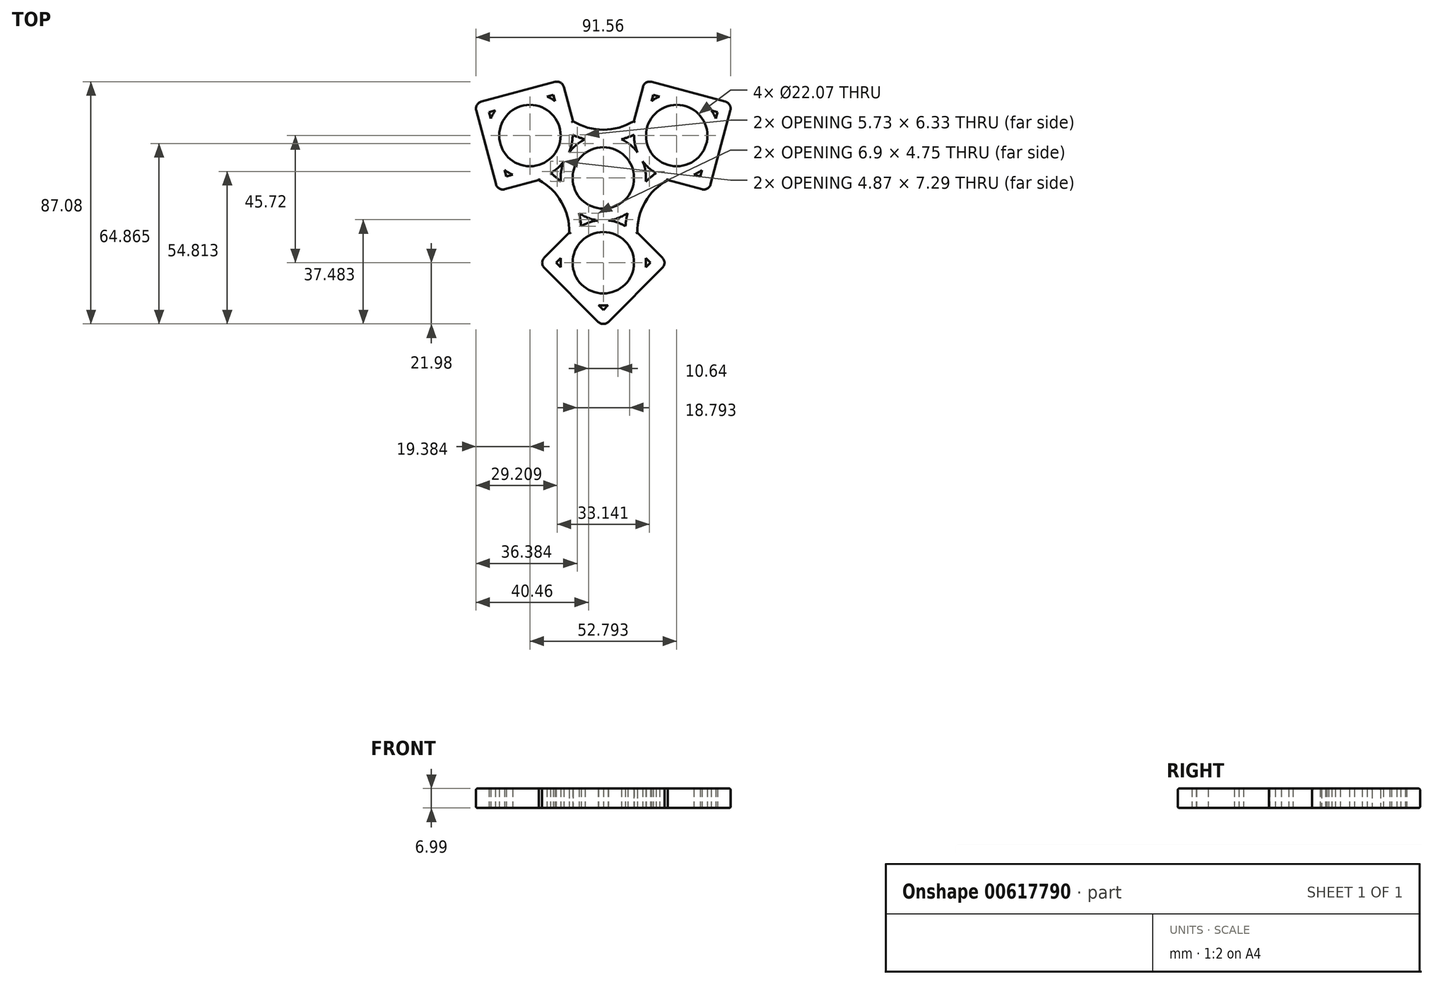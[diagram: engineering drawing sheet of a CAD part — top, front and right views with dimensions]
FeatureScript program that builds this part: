
annotation { "Feature Type Name" : "Feature", "Feature Type Description" : "" }
export const myFeature = defineFeature(function(context is Context, id is Id, definition is map)
    precondition{}
    {
        {
            var Q0;
            Q0=qCreatedBy(makeId("Top.planeOp"),FACE);
            var sketch = newSketch(context, id + "F0", { "sketchPlane" : qUnion([Q0])});
            skCircle(sketch, "E0", {"center": v(0, 0) * mm, "radius": 11.04 * mm});
            skLineSegment(sketch, "E1", {"start": v(0, 0) * mm, "end": v(26.4, 15.24) * mm});
            skLineSegment(sketch, "E2", {"start": v(0, 0) * mm, "end": v(-26.4, 15.24) * mm});
            skLineSegment(sketch, "E3", {"start": v(0, 0) * mm, "end": v(0, -30.48) * mm});
            skCircle(sketch, "E4", {"center": v(0, -30.48) * mm, "radius": 11.04 * mm});
            skCircle(sketch, "E5", {"center": v(-26.4, 15.24) * mm, "radius": 11.04 * mm});
            skCircle(sketch, "E6", {"center": v(26.4, 15.24) * mm, "radius": 11.04 * mm});
            skCircle(sketch, "E7.cCircle", {"center": v(-26.4, 15.24) * mm, "radius": 19.44 * mm, "construction": true});
            skLineSegment(sketch, "E7.0", {"start": v(-9.56, 5.52) * mm, "end": v(-36.12, -1.6) * mm});
            skLineSegment(sketch, "E7.1", {"start": v(-36.12, -1.6) * mm, "end": v(-43.24, 24.96) * mm});
            skLineSegment(sketch, "E7.2", {"start": v(-43.24, 24.96) * mm, "end": v(-16.67, 32.08) * mm});
            skLineSegment(sketch, "E7.3", {"start": v(-16.67, 32.08) * mm, "end": v(-9.56, 5.52) * mm});
            skCircle(sketch, "E8.cCircle", {"center": v(0, -30.48) * mm, "radius": 19.44 * mm, "construction": true});
            skPoint(sketch, "E8.cCircle.perimeterSnap0", {"position": v(0, -15.24) * mm});
            skLineSegment(sketch, "E8.0", {"start": v(0, -11.04) * mm, "end": v(19.44, -30.48) * mm});
            skPoint(sketch, "E8.0.startSnap0", {"position": v(0, -15.24) * mm});
            skLineSegment(sketch, "E8.1", {"start": v(19.44, -30.48) * mm, "end": v(0, -49.92) * mm});
            skLineSegment(sketch, "E8.2", {"start": v(0, -49.92) * mm, "end": v(-19.44, -30.48) * mm});
            skLineSegment(sketch, "E8.3", {"start": v(-19.44, -30.48) * mm, "end": v(0, -11.04) * mm});
            skCircle(sketch, "E9.cCircle", {"center": v(26.4, 15.24) * mm, "radius": 19.44 * mm, "construction": true});
            skLineSegment(sketch, "E9.0", {"start": v(9.56, 5.52) * mm, "end": v(16.67, 32.08) * mm});
            skLineSegment(sketch, "E9.1", {"start": v(16.67, 32.08) * mm, "end": v(43.24, 24.96) * mm});
            skLineSegment(sketch, "E9.2", {"start": v(43.24, 24.96) * mm, "end": v(36.12, -1.6) * mm});
            skLineSegment(sketch, "E9.3", {"start": v(36.12, -1.6) * mm, "end": v(9.56, 5.52) * mm});
            skArc(sketch, "E10", {"start": v(-9.72, -20.76) * mm, "mid": v(-12.84, -7.41) * mm, "end": v(-22.84, 1.96) * mm});
            skArc(sketch, "E11", {"start": v(22.84, 1.96) * mm, "mid": v(12.84, -7.41) * mm, "end": v(9.72, -20.76) * mm});
            skArc(sketch, "E12", {"start": v(-13.12, 18.8) * mm, "mid": v(0, 14.82) * mm, "end": v(13.12, 18.8) * mm});
            skCircle(sketch, "E13", {"center": v(0, 0) * mm, "radius": 14.82 * mm});
            skLineSegment(sketch, "E14.0", {"start": v(-46.35, 26.76) * mm, "end": v(-14.88, 35.19) * mm});
            skLineSegment(sketch, "E14.1", {"start": v(-37.91, -4.7) * mm, "end": v(-46.35, 26.76) * mm});
            skLineSegment(sketch, "E14.2", {"start": v(-6.45, 3.72) * mm, "end": v(-37.91, -4.7) * mm});
            skLineSegment(sketch, "E14.3", {"start": v(-14.88, 35.19) * mm, "end": v(-6.45, 3.72) * mm});
            skArc(sketch, "E15.0", {"start": v(-11.7, 20.91) * mm, "mid": v(0, 17.36) * mm, "end": v(11.7, 20.91) * mm});
            skLineSegment(sketch, "E16.0", {"start": v(6.45, 3.72) * mm, "end": v(14.88, 35.19) * mm});
            skLineSegment(sketch, "E16.1", {"start": v(37.91, -4.7) * mm, "end": v(6.45, 3.72) * mm});
            skLineSegment(sketch, "E16.2", {"start": v(46.35, 26.76) * mm, "end": v(37.91, -4.7) * mm});
            skLineSegment(sketch, "E16.3", {"start": v(14.88, 35.19) * mm, "end": v(46.35, 26.76) * mm});
            skLineSegment(sketch, "E17.0", {"start": v(-23.04, -30.48) * mm, "end": v(0, -7.44) * mm});
            skLineSegment(sketch, "E17.1", {"start": v(0, -53.52) * mm, "end": v(-23.04, -30.48) * mm});
            skLineSegment(sketch, "E17.2", {"start": v(23.04, -30.48) * mm, "end": v(0, -53.52) * mm});
            skLineSegment(sketch, "E17.3", {"start": v(0, -7.44) * mm, "end": v(23.04, -30.48) * mm});
            skArc(sketch, "E18.0", {"start": v(23.96, -0.32) * mm, "mid": v(15.03, -8.68) * mm, "end": v(12.26, -20.6) * mm});
            skArc(sketch, "E19.0", {"start": v(-12.26, -20.6) * mm, "mid": v(-15.03, -8.68) * mm, "end": v(-23.96, -0.32) * mm});
            skSolve(sketch);
        }
        {
            var Q0;
            {var subQ0=sQuery(id+"F0.wireOp",EDGE,"E10");var subQ1=sQuery(id+"F0.wireOp",EDGE,"E7.0");var subQ2=makeQuery(id+"F0.imprint","INTERSECT",VERTEX,{"derivedFrom":[subQ1,subQ0]});Q0=makeQuery(id+"F0.imprint","IMPRINT",FACE,{"disambiguationData":[TD([[makeQuery(id+"F0.imprint","IMPRINT",EDGE,{"disambiguationData":[TD([[subQ2,1.0]])],"derivedFrom":subQ1}),1.0]])]});}
            var Q1;
            {var subQ0=sQuery(id+"F0.wireOp",EDGE,"E12");var subQ1=sQuery(id+"F0.wireOp",EDGE,"E7.3");var subQ2=makeQuery(id+"F0.imprint","INTERSECT",VERTEX,{"derivedFrom":[subQ1,subQ0]});Q1=makeQuery(id+"F0.imprint","IMPRINT",FACE,{"disambiguationData":[TD([[makeQuery(id+"F0.imprint","IMPRINT",EDGE,{"disambiguationData":[TD([[subQ2,-1.0]])],"derivedFrom":subQ1}),1.0]])]});}
            var Q2;
            {var subQ0=sQuery(id+"F0.wireOp",EDGE,"E11");var subQ1=sQuery(id+"F0.wireOp",EDGE,"E8.0");var subQ2=makeQuery(id+"F0.imprint","INTERSECT",VERTEX,{"derivedFrom":[subQ1,subQ0]});Q2=makeQuery(id+"F0.imprint","IMPRINT",FACE,{"disambiguationData":[TD([[makeQuery(id+"F0.imprint","IMPRINT",EDGE,{"disambiguationData":[TD([[subQ2,1.0]])],"derivedFrom":subQ1}),1.0]])]});}
            var Q3;
            {var subQ0=sQuery(id+"F0.wireOp",EDGE,"E10");var subQ1=sQuery(id+"F0.wireOp",EDGE,"E8.3");var subQ2=makeQuery(id+"F0.imprint","INTERSECT",VERTEX,{"derivedFrom":[subQ1,subQ0]});Q3=makeQuery(id+"F0.imprint","IMPRINT",FACE,{"disambiguationData":[TD([[makeQuery(id+"F0.imprint","IMPRINT",EDGE,{"disambiguationData":[TD([[subQ2,-1.0]])],"derivedFrom":subQ1}),1.0]])]});}
            var Q4;
            {var subQ0=sQuery(id+"F0.wireOp",EDGE,"E12");var subQ1=sQuery(id+"F0.wireOp",EDGE,"E9.0");var subQ2=makeQuery(id+"F0.imprint","INTERSECT",VERTEX,{"derivedFrom":[subQ1,subQ0]});Q4=makeQuery(id+"F0.imprint","IMPRINT",FACE,{"disambiguationData":[TD([[makeQuery(id+"F0.imprint","IMPRINT",EDGE,{"disambiguationData":[TD([[subQ2,1.0]])],"derivedFrom":subQ1}),1.0]])]});}
            var Q5;
            {var subQ0=sQuery(id+"F0.wireOp",EDGE,"E11");var subQ1=sQuery(id+"F0.wireOp",EDGE,"E9.3");var subQ2=makeQuery(id+"F0.imprint","INTERSECT",VERTEX,{"derivedFrom":[subQ1,subQ0]});Q5=makeQuery(id+"F0.imprint","IMPRINT",FACE,{"disambiguationData":[TD([[makeQuery(id+"F0.imprint","IMPRINT",EDGE,{"disambiguationData":[TD([[subQ2,-1.0]])],"derivedFrom":subQ1}),1.0]])]});}
            var Q6;
            {var subQ3=sQuery(id+"F0.wireOp",EDGE,"E13");var subQ8=makeQuery(id+"F0.imprint","INTERSECT",VERTEX,{"derivedFrom":[sQuery(id+"F0.wireOp",EDGE,"E11"),subQ3]});Q6=makeQuery(id+"F0.imprint","IMPRINT",FACE,{"disambiguationData":[TD([[makeQuery(id+"F0.imprint","IMPRINT",EDGE,{"disambiguationData":[TD([[subQ8,1.0]])],"derivedFrom":subQ3}),1.0]])]});}
            var Q7;
            Q7=makeQuery(id+"F0.imprint","IMPRINT",FACE,{"disambiguationData":[TD([[makeQuery(id+"F0.imprint","IMPRINT",EDGE,{"derivedFrom":sQuery(id+"F0.wireOp",EDGE,"E4")}),-1.0]])]});
            var Q8;
            Q8=makeQuery(id+"F0.imprint","IMPRINT",FACE,{"disambiguationData":[TD([[makeQuery(id+"F0.imprint","IMPRINT",EDGE,{"derivedFrom":sQuery(id+"F0.wireOp",EDGE,"E5")}),-1.0]])]});
            var Q9;
            Q9=makeQuery(id+"F0.imprint","IMPRINT",FACE,{"disambiguationData":[TD([[makeQuery(id+"F0.imprint","IMPRINT",EDGE,{"derivedFrom":sQuery(id+"F0.wireOp",EDGE,"E6")}),-1.0]])]});
            var Q10;
            {var subQ1=sQuery(id+"F0.wireOp",EDGE,"E3");var subQ3=sQuery(id+"F0.wireOp",EDGE,"E13");var subQ4=makeQuery(id+"F0.imprint","INTERSECT",VERTEX,{"derivedFrom":[subQ1,subQ3]});Q10=makeQuery(id+"F0.imprint","IMPRINT",FACE,{"disambiguationData":[TD([[makeQuery(id+"F0.imprint","IMPRINT",EDGE,{"disambiguationData":[TD([[subQ4,-1.0]])],"derivedFrom":subQ3}),1.0]])]});}
            var Q11;
            {var subQ1=sQuery(id+"F0.wireOp",EDGE,"E3");var subQ3=sQuery(id+"F0.wireOp",EDGE,"E13");var subQ4=makeQuery(id+"F0.imprint","INTERSECT",VERTEX,{"derivedFrom":[subQ1,subQ3]});Q11=makeQuery(id+"F0.imprint","IMPRINT",FACE,{"disambiguationData":[TD([[makeQuery(id+"F0.imprint","IMPRINT",EDGE,{"disambiguationData":[TD([[subQ4,1.0]])],"derivedFrom":subQ3}),1.0]])]});}
            var Q12;
            {var subQ1=sQuery(id+"F0.wireOp",EDGE,"E1");var subQ3=sQuery(id+"F0.wireOp",EDGE,"E13");var subQ4=makeQuery(id+"F0.imprint","INTERSECT",VERTEX,{"derivedFrom":[subQ1,subQ3]});Q12=makeQuery(id+"F0.imprint","IMPRINT",FACE,{"disambiguationData":[TD([[makeQuery(id+"F0.imprint","IMPRINT",EDGE,{"disambiguationData":[TD([[subQ4,1.0]])],"derivedFrom":subQ3}),1.0]])]});}
            var Q13;
            {var subQ1=sQuery(id+"F0.wireOp",EDGE,"E1");var subQ3=sQuery(id+"F0.wireOp",EDGE,"E13");var subQ4=makeQuery(id+"F0.imprint","INTERSECT",VERTEX,{"derivedFrom":[subQ1,subQ3]});Q13=makeQuery(id+"F0.imprint","IMPRINT",FACE,{"disambiguationData":[TD([[makeQuery(id+"F0.imprint","IMPRINT",EDGE,{"disambiguationData":[TD([[subQ4,-1.0]])],"derivedFrom":subQ3}),1.0]])]});}
            var Q14;
            {var subQ1=sQuery(id+"F0.wireOp",EDGE,"E2");var subQ3=sQuery(id+"F0.wireOp",EDGE,"E13");var subQ4=makeQuery(id+"F0.imprint","INTERSECT",VERTEX,{"derivedFrom":[subQ1,subQ3]});Q14=makeQuery(id+"F0.imprint","IMPRINT",FACE,{"disambiguationData":[TD([[makeQuery(id+"F0.imprint","IMPRINT",EDGE,{"disambiguationData":[TD([[subQ4,1.0]])],"derivedFrom":subQ3}),1.0]])]});}
            var Q15;
            {var subQ3=sQuery(id+"F0.wireOp",EDGE,"E13");var subQ5=makeQuery(id+"F0.imprint","INTERSECT",VERTEX,{"derivedFrom":[sQuery(id+"F0.wireOp",EDGE,"E12"),subQ3]});Q15=makeQuery(id+"F0.imprint","IMPRINT",FACE,{"disambiguationData":[TD([[makeQuery(id+"F0.imprint","IMPRINT",EDGE,{"disambiguationData":[TD([[subQ5,1.0]])],"derivedFrom":subQ3}),1.0]])]});}
            var Q16;
            {var subQ0=sQuery(id+"F0.wireOp",EDGE,"E13");var subQ1=makeQuery(id+"F0.imprint","INTERSECT",VERTEX,{"derivedFrom":[sQuery(id+"F0.wireOp",EDGE,"E10"),subQ0]});Q16=makeQuery(id+"F0.imprint","IMPRINT",FACE,{"disambiguationData":[TD([[makeQuery(id+"F0.imprint","IMPRINT",EDGE,{"disambiguationData":[TD([[subQ1,1.0]])],"derivedFrom":subQ0}),1.0]])]});}
            var Q17;
            {var subQ1=sQuery(id+"F0.wireOp",EDGE,"E2");var subQ3=sQuery(id+"F0.wireOp",EDGE,"E13");var subQ4=makeQuery(id+"F0.imprint","INTERSECT",VERTEX,{"derivedFrom":[subQ1,subQ3]});Q17=makeQuery(id+"F0.imprint","IMPRINT",FACE,{"disambiguationData":[TD([[makeQuery(id+"F0.imprint","IMPRINT",EDGE,{"disambiguationData":[TD([[subQ4,-1.0]])],"derivedFrom":subQ3}),1.0]])]});}
            var Q18;
            {var subQ7=sQuery(id+"F0.wireOp",EDGE,"E7.1");Q18=makeQuery(id+"F0.imprint","IMPRINT",FACE,{"disambiguationData":[TD([[makeQuery(id+"F0.imprint","IMPRINT",EDGE,{"derivedFrom":subQ7}),1.0]])]});}
            var Q19;
            {var subQ3=sQuery(id+"F0.wireOp",EDGE,"E10");var subQ6=sQuery(id+"F0.wireOp",EDGE,"E17.0");var subQ8=makeQuery(id+"F0.imprint","INTERSECT",VERTEX,{"derivedFrom":[subQ3,subQ6]});Q19=makeQuery(id+"F0.imprint","IMPRINT",FACE,{"disambiguationData":[TD([[makeQuery(id+"F0.imprint","IMPRINT",EDGE,{"disambiguationData":[TD([[subQ8,-1.0]])],"derivedFrom":subQ3}),1.0]])]});}
            var Q20;
            {var subQ1=sQuery(id+"F0.wireOp",EDGE,"E14.3");var subQ5=sQuery(id+"F0.wireOp",EDGE,"E12");var subQ6=makeQuery(id+"F0.imprint","INTERSECT",VERTEX,{"derivedFrom":[subQ5,subQ1]});Q20=makeQuery(id+"F0.imprint","IMPRINT",FACE,{"disambiguationData":[TD([[makeQuery(id+"F0.imprint","IMPRINT",EDGE,{"disambiguationData":[TD([[subQ6,-1.0]])],"derivedFrom":subQ5}),1.0]])]});}
            var Q21;
            {var subQ0=sQuery(id+"F0.wireOp",EDGE,"E7.3");var subQ5=sQuery(id+"F0.wireOp",EDGE,"E13");var subQ6=makeQuery(id+"F0.imprint","INTERSECT",VERTEX,{"derivedFrom":[subQ0,subQ5]});Q21=makeQuery(id+"F0.imprint","IMPRINT",FACE,{"disambiguationData":[TD([[makeQuery(id+"F0.imprint","IMPRINT",EDGE,{"disambiguationData":[TD([[subQ6,1.0]])],"derivedFrom":subQ5}),1.0]])]});}
            var Q22;
            {var subQ0=sQuery(id+"F0.wireOp",EDGE,"E7.0");var subQ5=sQuery(id+"F0.wireOp",EDGE,"E13");var subQ6=makeQuery(id+"F0.imprint","INTERSECT",VERTEX,{"derivedFrom":[subQ0,subQ5]});Q22=makeQuery(id+"F0.imprint","IMPRINT",FACE,{"disambiguationData":[TD([[makeQuery(id+"F0.imprint","IMPRINT",EDGE,{"disambiguationData":[TD([[subQ6,-1.0]])],"derivedFrom":subQ5}),1.0]])]});}
            var Q23;
            {var subQ14=sQuery(id+"F0.wireOp",EDGE,"E9.1");Q23=makeQuery(id+"F0.imprint","IMPRINT",FACE,{"disambiguationData":[TD([[makeQuery(id+"F0.imprint","IMPRINT",EDGE,{"derivedFrom":subQ14}),1.0]])]});}
            var Q24;
            {var subQ0=sQuery(id+"F0.wireOp",EDGE,"E9.0");var subQ5=sQuery(id+"F0.wireOp",EDGE,"E13");var subQ6=makeQuery(id+"F0.imprint","INTERSECT",VERTEX,{"derivedFrom":[subQ0,subQ5]});Q24=makeQuery(id+"F0.imprint","IMPRINT",FACE,{"disambiguationData":[TD([[makeQuery(id+"F0.imprint","IMPRINT",EDGE,{"disambiguationData":[TD([[subQ6,-1.0]])],"derivedFrom":subQ5}),1.0]])]});}
            var Q25;
            {var subQ0=sQuery(id+"F0.wireOp",EDGE,"E9.3");var subQ5=sQuery(id+"F0.wireOp",EDGE,"E13");var subQ6=makeQuery(id+"F0.imprint","INTERSECT",VERTEX,{"derivedFrom":[subQ0,subQ5]});Q25=makeQuery(id+"F0.imprint","IMPRINT",FACE,{"disambiguationData":[TD([[makeQuery(id+"F0.imprint","IMPRINT",EDGE,{"disambiguationData":[TD([[subQ6,1.0]])],"derivedFrom":subQ5}),1.0]])]});}
            var Q26;
            {var subQ0=sQuery(id+"F0.wireOp",EDGE,"E8.3");var subQ5=sQuery(id+"F0.wireOp",EDGE,"E13");var subQ6=makeQuery(id+"F0.imprint","INTERSECT",VERTEX,{"derivedFrom":[subQ0,subQ5]});Q26=makeQuery(id+"F0.imprint","IMPRINT",FACE,{"disambiguationData":[TD([[makeQuery(id+"F0.imprint","IMPRINT",EDGE,{"disambiguationData":[TD([[subQ6,1.0]])],"derivedFrom":subQ5}),1.0]])]});}
            var Q27;
            {var subQ0=sQuery(id+"F0.wireOp",EDGE,"E8.0");var subQ5=sQuery(id+"F0.wireOp",EDGE,"E13");var subQ6=makeQuery(id+"F0.imprint","INTERSECT",VERTEX,{"derivedFrom":[subQ0,subQ5]});Q27=makeQuery(id+"F0.imprint","IMPRINT",FACE,{"disambiguationData":[TD([[makeQuery(id+"F0.imprint","IMPRINT",EDGE,{"disambiguationData":[TD([[subQ6,-1.0]])],"derivedFrom":subQ5}),1.0]])]});}
            var Q28;
            {var subQ6=sQuery(id+"F0.wireOp",EDGE,"E8.1");Q28=makeQuery(id+"F0.imprint","IMPRINT",FACE,{"disambiguationData":[TD([[makeQuery(id+"F0.imprint","IMPRINT",EDGE,{"derivedFrom":subQ6}),1.0]])]});}
            var Q29;
            {var subQ1=sQuery(id+"F0.wireOp",EDGE,"E16.1");var subQ3=sQuery(id+"F0.wireOp",EDGE,"E11");var subQ4=makeQuery(id+"F0.imprint","INTERSECT",VERTEX,{"derivedFrom":[subQ3,subQ1]});Q29=makeQuery(id+"F0.imprint","IMPRINT",FACE,{"disambiguationData":[TD([[makeQuery(id+"F0.imprint","IMPRINT",EDGE,{"disambiguationData":[TD([[subQ4,-1.0]])],"derivedFrom":subQ3}),1.0]])]});}
            var Q30;
            {var subQ0=sQuery(id+"F0.wireOp",EDGE,"E14.3");var subQ1=sQuery(id+"F0.wireOp",EDGE,"E12");var subQ2=makeQuery(id+"F0.imprint","INTERSECT",VERTEX,{"derivedFrom":[subQ1,subQ0]});Q30=makeQuery(id+"F0.imprint","IMPRINT",FACE,{"disambiguationData":[TD([[makeQuery(id+"F0.imprint","IMPRINT",EDGE,{"disambiguationData":[TD([[subQ2,-1.0]])],"derivedFrom":subQ1}),-1.0]])]});}
            var Q31;
            {var subQ0=sQuery(id+"F0.wireOp",EDGE,"E13");var subQ1=sQuery(id+"F0.wireOp",EDGE,"E12");var subQ2=makeQuery(id+"F0.imprint","INTERSECT",VERTEX,{"derivedFrom":[subQ1,subQ0]});Q31=makeQuery(id+"F0.imprint","IMPRINT",FACE,{"disambiguationData":[TD([[makeQuery(id+"F0.imprint","IMPRINT",EDGE,{"disambiguationData":[TD([[subQ2,-1.0]])],"derivedFrom":subQ1}),-1.0]])]});}
            var Q32;
            {var subQ0=sQuery(id+"F0.wireOp",EDGE,"E16.1");var subQ1=sQuery(id+"F0.wireOp",EDGE,"E11");var subQ2=makeQuery(id+"F0.imprint","INTERSECT",VERTEX,{"derivedFrom":[subQ1,subQ0]});Q32=makeQuery(id+"F0.imprint","IMPRINT",FACE,{"disambiguationData":[TD([[makeQuery(id+"F0.imprint","IMPRINT",EDGE,{"disambiguationData":[TD([[subQ2,-1.0]])],"derivedFrom":subQ1}),-1.0]])]});}
            var Q33;
            {var subQ0=sQuery(id+"F0.wireOp",EDGE,"E13");var subQ1=sQuery(id+"F0.wireOp",EDGE,"E11");var subQ2=makeQuery(id+"F0.imprint","INTERSECT",VERTEX,{"derivedFrom":[subQ1,subQ0]});Q33=makeQuery(id+"F0.imprint","IMPRINT",FACE,{"disambiguationData":[TD([[makeQuery(id+"F0.imprint","IMPRINT",EDGE,{"disambiguationData":[TD([[subQ2,-1.0]])],"derivedFrom":subQ1}),-1.0]])]});}
            var Q34;
            {var subQ0=sQuery(id+"F0.wireOp",EDGE,"E17.0");var subQ1=sQuery(id+"F0.wireOp",EDGE,"E10");var subQ2=makeQuery(id+"F0.imprint","INTERSECT",VERTEX,{"derivedFrom":[subQ1,subQ0]});Q34=makeQuery(id+"F0.imprint","IMPRINT",FACE,{"disambiguationData":[TD([[makeQuery(id+"F0.imprint","IMPRINT",EDGE,{"disambiguationData":[TD([[subQ2,-1.0]])],"derivedFrom":subQ1}),-1.0]])]});}
            var Q35;
            {var subQ0=sQuery(id+"F0.wireOp",EDGE,"E13");var subQ1=sQuery(id+"F0.wireOp",EDGE,"E10");var subQ2=makeQuery(id+"F0.imprint","INTERSECT",VERTEX,{"derivedFrom":[subQ1,subQ0]});Q35=makeQuery(id+"F0.imprint","IMPRINT",FACE,{"disambiguationData":[TD([[makeQuery(id+"F0.imprint","IMPRINT",EDGE,{"disambiguationData":[TD([[subQ2,-1.0]])],"derivedFrom":subQ1}),-1.0]])]});}
            extrude(context, id + "F1", {"entities" : qUnion([Q0, Q1, Q2, Q3, Q4, Q5, Q6, Q7, Q8, Q9, Q10, Q11, Q12, Q13, Q14, Q15, Q16, Q17, Q18, Q19, Q20, Q21, Q22, Q23, Q24, Q25, Q26, Q27, Q28, Q29, Q30, Q31, Q32, Q33, Q34, Q35]), "depth" : 7 * mm, "offsetDistance" : 25.4 * mm});
        }
        {
            var Q0;
            Q0=makeQuery(id+"F1.opExtrude","CAP_FACE",FACE,{"disambiguationData":[OSD([sQuery(id+"F0.wireOp",EDGE,"E0"),sQuery(id+"F0.wireOp",EDGE,"E4"),sQuery(id+"F0.wireOp",EDGE,"E5"),sQuery(id+"F0.wireOp",EDGE,"E6"),sQuery(id+"F0.wireOp",EDGE,"E14.0"),sQuery(id+"F0.wireOp",EDGE,"E14.1"),sQuery(id+"F0.wireOp",EDGE,"E14.2"),sQuery(id+"F0.wireOp",EDGE,"E14.3"),sQuery(id+"F0.wireOp",EDGE,"E15.0"),sQuery(id+"F0.wireOp",EDGE,"E16.0"),sQuery(id+"F0.wireOp",EDGE,"E16.1"),sQuery(id+"F0.wireOp",EDGE,"E16.2"),sQuery(id+"F0.wireOp",EDGE,"E16.3"),sQuery(id+"F0.wireOp",EDGE,"E17.0"),sQuery(id+"F0.wireOp",EDGE,"E17.1"),sQuery(id+"F0.wireOp",EDGE,"E17.2"),sQuery(id+"F0.wireOp",EDGE,"E17.3"),sQuery(id+"F0.wireOp",EDGE,"E18.0"),sQuery(id+"F0.wireOp",EDGE,"E19.0")])],"isStart":false});
            var Q1;
            Q1=makeQuery(id+"F1.opExtrude","CAP_FACE",FACE,{"disambiguationData":[OSD([sQuery(id+"F0.wireOp",EDGE,"E0"),sQuery(id+"F0.wireOp",EDGE,"E4"),sQuery(id+"F0.wireOp",EDGE,"E5"),sQuery(id+"F0.wireOp",EDGE,"E6"),sQuery(id+"F0.wireOp",EDGE,"E14.0"),sQuery(id+"F0.wireOp",EDGE,"E14.1"),sQuery(id+"F0.wireOp",EDGE,"E14.2"),sQuery(id+"F0.wireOp",EDGE,"E14.3"),sQuery(id+"F0.wireOp",EDGE,"E15.0"),sQuery(id+"F0.wireOp",EDGE,"E16.0"),sQuery(id+"F0.wireOp",EDGE,"E16.1"),sQuery(id+"F0.wireOp",EDGE,"E16.2"),sQuery(id+"F0.wireOp",EDGE,"E16.3"),sQuery(id+"F0.wireOp",EDGE,"E17.0"),sQuery(id+"F0.wireOp",EDGE,"E17.1"),sQuery(id+"F0.wireOp",EDGE,"E17.2"),sQuery(id+"F0.wireOp",EDGE,"E17.3"),sQuery(id+"F0.wireOp",EDGE,"E18.0"),sQuery(id+"F0.wireOp",EDGE,"E19.0")])],"isStart":true});
            shell(context, id + "F2", {"entities" : qUnion([Q0, Q1]), "thickness" : 4.32 * mm});
        }
        {
            var Q0;
            Q0=makeQuery(id+"F1.opExtrude","SWEPT_EDGE",EDGE,{"disambiguationData":[OSD([sQuery(id+"F0.wireOp",EDGE,"E14.1"),sQuery(id+"F0.wireOp",EDGE,"E14.2")])]});
            var Q1;
            Q1=makeQuery(id+"F1.opExtrude","SWEPT_EDGE",EDGE,{"disambiguationData":[OSD([sQuery(id+"F0.wireOp",EDGE,"E17.0"),sQuery(id+"F0.wireOp",EDGE,"E17.1")])]});
            var Q2;
            Q2=makeQuery(id+"F1.opExtrude","SWEPT_EDGE",EDGE,{"disambiguationData":[OSD([sQuery(id+"F0.wireOp",EDGE,"E17.1"),sQuery(id+"F0.wireOp",EDGE,"E17.2")])]});
            var Q3;
            Q3=makeQuery(id+"F1.opExtrude","SWEPT_EDGE",EDGE,{"disambiguationData":[OSD([sQuery(id+"F0.wireOp",EDGE,"E14.0"),sQuery(id+"F0.wireOp",EDGE,"E14.1")])]});
            var Q4;
            Q4=makeQuery(id+"F1.opExtrude","SWEPT_EDGE",EDGE,{"disambiguationData":[OSD([sQuery(id+"F0.wireOp",EDGE,"E14.0"),sQuery(id+"F0.wireOp",EDGE,"E14.3")])]});
            var Q5;
            Q5=makeQuery(id+"F1.opExtrude","SWEPT_EDGE",EDGE,{"disambiguationData":[OSD([sQuery(id+"F0.wireOp",EDGE,"E16.0"),sQuery(id+"F0.wireOp",EDGE,"E16.3")])]});
            var Q6;
            Q6=makeQuery(id+"F1.opExtrude","SWEPT_EDGE",EDGE,{"disambiguationData":[OSD([sQuery(id+"F0.wireOp",EDGE,"E16.2"),sQuery(id+"F0.wireOp",EDGE,"E16.3")])]});
            var Q7;
            Q7=makeQuery(id+"F1.opExtrude","SWEPT_EDGE",EDGE,{"disambiguationData":[OSD([sQuery(id+"F0.wireOp",EDGE,"E16.1"),sQuery(id+"F0.wireOp",EDGE,"E16.2")])]});
            var Q8;
            Q8=makeQuery(id+"F1.opExtrude","SWEPT_EDGE",EDGE,{"disambiguationData":[OSD([sQuery(id+"F0.wireOp",EDGE,"E17.2"),sQuery(id+"F0.wireOp",EDGE,"E17.3")])]});
            fillet(context, id + "F3", {"entities" : qUnion([Q0, Q1, Q2, Q3, Q4, Q5, Q6, Q7, Q8]), "radius" : 2.54 * mm, "tangentPropagation" : true, "allowEdgeOverflow" : false});
        }
        {
            var Q0;
            Q0=makeQuery(id+"F1.opExtrude","CAP_EDGE",EDGE,{"disambiguationData":[OSD([sQuery(id+"F0.wireOp",EDGE,"E14.0")])],"isStart":false});
            var Q1;
            Q1=makeQuery(id+"F1.opExtrude","CAP_EDGE",EDGE,{"disambiguationData":[OSD([sQuery(id+"F0.wireOp",EDGE,"E15.0")])],"isStart":false});
            var Q2;
            Q2=makeQuery(id+"F1.opExtrude","CAP_EDGE",EDGE,{"disambiguationData":[OSD([sQuery(id+"F0.wireOp",EDGE,"E16.0")])],"isStart":false});
            var Q3;
            Q3=makeQuery(id+"F1.opExtrude","CAP_EDGE",EDGE,{"disambiguationData":[OSD([sQuery(id+"F0.wireOp",EDGE,"E18.0")])],"isStart":false});
            var Q4;
            Q4=makeQuery(id+"F1.opExtrude","CAP_EDGE",EDGE,{"disambiguationData":[OSD([sQuery(id+"F0.wireOp",EDGE,"E17.3")])],"isStart":false});
            var Q5;
            Q5=makeQuery(id+"F1.opExtrude","CAP_EDGE",EDGE,{"disambiguationData":[OSD([sQuery(id+"F0.wireOp",EDGE,"E19.0")])],"isStart":false});
            fillet(context, id + "F4", {"entities" : qUnion([Q0, Q1, Q2, Q3, Q4, Q5]), "radius" : 0.5 * mm, "tangentPropagation" : true, "allowEdgeOverflow" : false});
        }
        {
            var Q0;
            Q0=makeQuery(id+"F1.opExtrude","CAP_EDGE",EDGE,{"disambiguationData":[OSD([sQuery(id+"F0.wireOp",EDGE,"E17.0")])],"isStart":true});
            var Q1;
            Q1=makeQuery(id+"F1.opExtrude","CAP_EDGE",EDGE,{"disambiguationData":[OSD([sQuery(id+"F0.wireOp",EDGE,"E19.0")])],"isStart":true});
            var Q2;
            Q2=makeQuery(id+"F1.opExtrude","CAP_EDGE",EDGE,{"disambiguationData":[OSD([sQuery(id+"F0.wireOp",EDGE,"E14.2")])],"isStart":true});
            var Q3;
            Q3=makeQuery(id+"F1.opExtrude","CAP_EDGE",EDGE,{"disambiguationData":[OSD([sQuery(id+"F0.wireOp",EDGE,"E15.0")])],"isStart":true});
            var Q4;
            Q4=makeQuery(id+"F1.opExtrude","CAP_EDGE",EDGE,{"disambiguationData":[OSD([sQuery(id+"F0.wireOp",EDGE,"E16.0")])],"isStart":true});
            var Q5;
            Q5=makeQuery(id+"F1.opExtrude","CAP_EDGE",EDGE,{"disambiguationData":[OSD([sQuery(id+"F0.wireOp",EDGE,"E18.0")])],"isStart":true});
            fillet(context, id + "F5", {"entities" : qUnion([Q0, Q1, Q2, Q3, Q4, Q5]), "radius" : 0.5 * mm, "tangentPropagation" : true, "allowEdgeOverflow" : false});
        }
    });
